# Revit family: Building-FlushMountingEnclosures-GEWISS-24SC-UNDERFLOOR_BOXES_HOLLOW_LID
name_source: partatom
category: Apparecchi elettrici
revit_build: Autodesk Revit 2016 (Build: 20161004_0715(x64)
units: mm (PartAtom-declared; Revit-internal decimal feet)

## family parameters
Condiviso = Sì
Host = Superficie
Mantenere orientamento annotazione = Sì
Punto di calcolo locali = Sì
Quota connettore circolare = Usa diametro
Taglio con vuoti quando caricato = No
Tipo di parte = Normale

## types (2) — shared parameters
Catalogue = BUILDING
Catalogue Range = 24SC
Characteristics = Halogen free
Electrocod = 200
Glow Wire Test = 850°C
IDF = 3b5d9fb5-c28b-476e-befd-bd9af68ce945
IDT = 378438b0-1c43-443a-b718-4098a61d4167
Immagine tipo = GW24602.jpg
Lid = Cable
Operating temperature = -5 +45 °C
Produttore = GEWISS S.p.A.
Prospetto di default = 1219 mm
SEO = Underfloor box
TIPO = Torrette a Scomparsa coperchi_GENERICO : GW24602 Torretta a scomparsa 20p con coperchio cavo
Technical sheet = https://www.gewiss.com
URL = https://www.gewiss.com
Version file RFA = 19.0

## per-type parameters (varying)
| type | Descrizione | EAN code | Internal modularity | Modello | No. of supports | Outer dim. LxHxD (mm) |
| GW24601 - Underfloor outlet box 10P hollow cover | UNDERFLOOR OUTLET BOX 10P HOLLOW COVER | 8011564759596 | 10 SYSTEM modules | GW24601 | 2 supports with 5 System mod. | 212x98x320 |
| GW24602 - Underfloor outlet box 20P hollow cover | UNDERFLOOR OUTLET BOX 20P HOLLOW COVER | 8011564759602 | 20 SYSTEM modules | GW24602 | 4 supports with 5 System mod. | 364x98x320 |

## geometry (parser evidence)
native form markers: Blend x2, Sweep x1
no freeform markers — native parametric forms only
